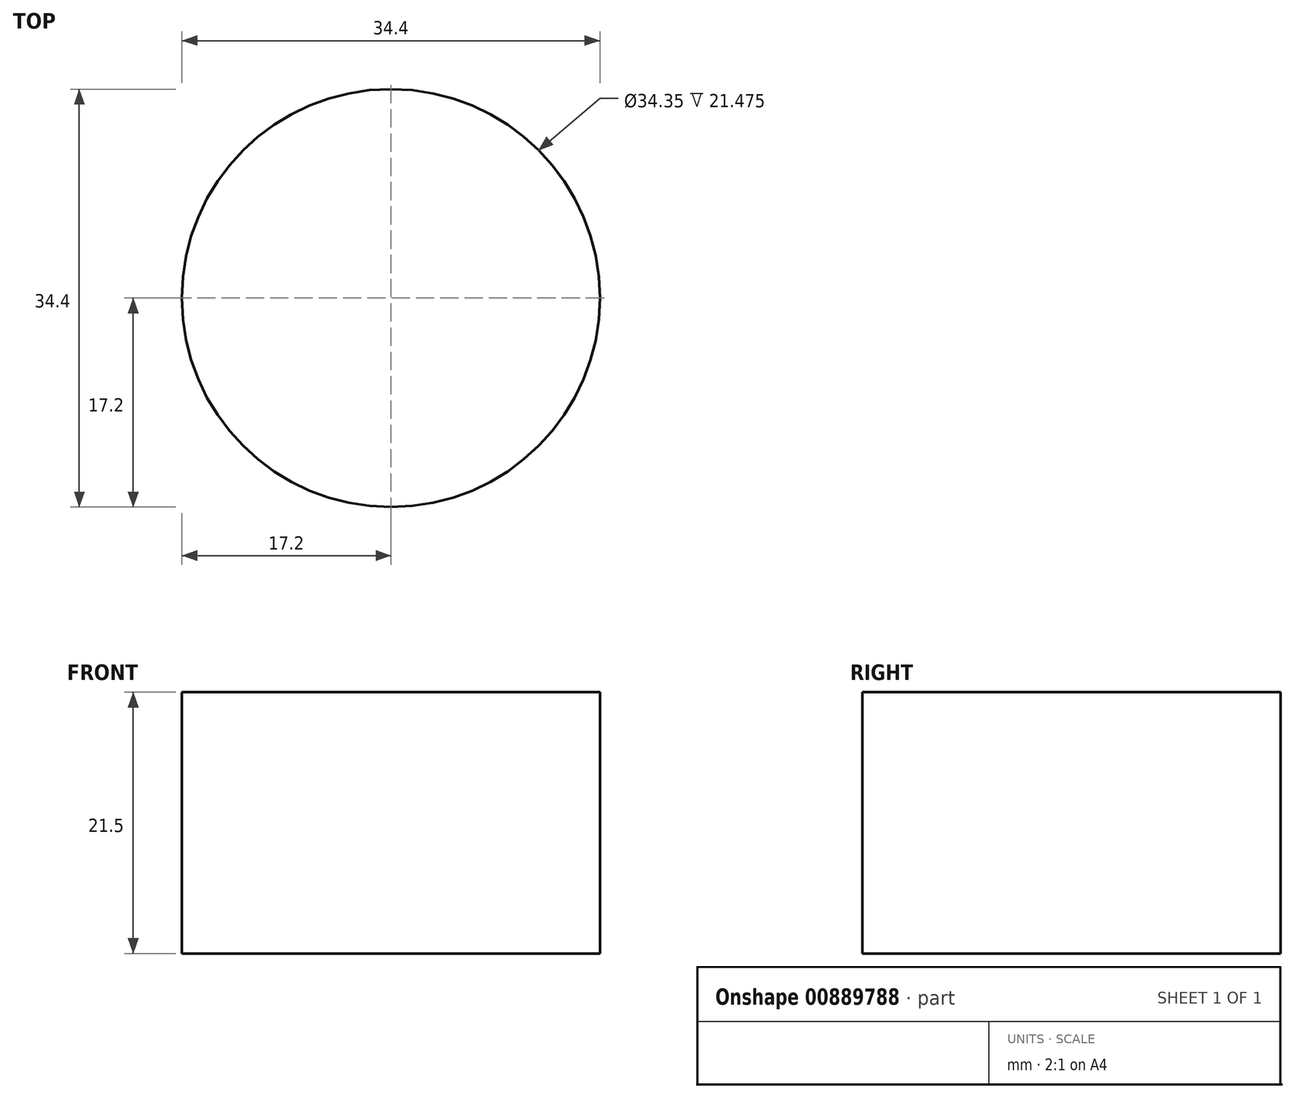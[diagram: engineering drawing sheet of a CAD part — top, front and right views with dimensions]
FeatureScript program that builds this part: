
annotation { "Feature Type Name" : "Feature", "Feature Type Description" : "" }
export const myFeature = defineFeature(function(context is Context, id is Id, definition is map)
    precondition{}
    {
        {
            var Q0;
            Q0=qCreatedBy(makeId("Top.planeOp"),FACE);
            var sketch = newSketch(context, id + "F0", { "sketchPlane" : qUnion([Q0])});
            skCircle(sketch, "E0", {"center": v(0, 0) * mm, "radius": 17.2 * mm});
            skSolve(sketch);
        }
        {
            var Q0;
            Q0=makeQuery(id+"FFGotPLcMoUgvG6_0.imprint","IMPRINT",FACE,{"disambiguationData":[TD([[makeQuery(id+"FFGotPLcMoUgvG6_0.imprint","IMPRINT",EDGE,{"derivedFrom":sQuery(id+"FFGotPLcMoUgvG6_0.wireOp",EDGE,"5n9h9rbT-I2yB-HAuP-Ihzt-tGG4yHLKOiWa")}),1.0]])]});
            var Q1;
            Q1 = qSketchRegion(id + "F0", true);
            var Q2;
            Q2=sQuery(id+"F0.wireOp",EDGE,"E0");
            var Q3;
            Q3=sQuery(id+"FFGotPLcMoUgvG6_0.wireOp",EDGE,"5n9h9rbT-I2yB-HAuP-Ihzt-tGG4yHLKOiWa");
            extrude(context, id + "F1", {"entities" : qUnion([Q0, Q1]), "surfaceOperationType" : NewSurfaceOperationType.ADD, "surfaceEntities" : qUnion([Q2, Q3]), "oppositeDirection" : true, "depth" : 21.5 * mm, "offsetDistance" : 25 * mm});
        }
        {
            var Q0;
            Q0=makeQuery(id+"F1.opExtrude","CAP_FACE",FACE,{"disambiguationData":[OSD([sQuery(id+"F0.wireOp",EDGE,"E0")])],"isStart":false});
            shell(context, id + "F2", {"entities" : qUnion([Q0]), "thickness" : 0.03 * mm});
        }
    });
